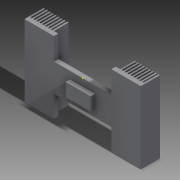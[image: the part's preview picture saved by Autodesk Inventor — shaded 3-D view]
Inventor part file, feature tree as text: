
AUTODESK INVENTOR PART (.ipt)
format: ipt  version: 2015 (Build 190159000, 159)  size: 207,360 bytes
history: native  units: in
note: dims shown in document units (in); Inventor stores cm internally (conversion verified against a paired STEP export)
features: extrude x3, sketch x3
ambient origin geometry x8: Origin, YZ Plane, XZ Plane, XY Plane, X Axis, Y Axis, Z Axis, Center Point
bodies: Body1 (feature_tree)
feature tree (6):
  extrude  "Extrusion2"  Depth=0.6693in
  extrude  "Extrusion3"  Depth=0.1181in TaperAngle=0.0deg
  sketch  "Sketch6"  dims[d13=0.3543in d14=0.1181in d15=0.0in]
  extrude  "Extrusion6"  Depth=0.1969in
  sketch  "Sketch2"  dims[d10=0.1181in d11=0.0in d12=0.6693in]
  sketch  "Sketch7"  dims[d16=0.4331in d17=0.1969in d18=1.5354in d39=0.748in d53=1.9291in d54=0.0in d55=1.5354in d56=1.1811in d57=0.5906in d58=0.7874in d59=0.3937in d60=0.0394in d69=3.5433in d71=0.0787in d72=0.3937in d74=0.3937in d76=3.1102in d77=0.1181in d78=1.9291in]
